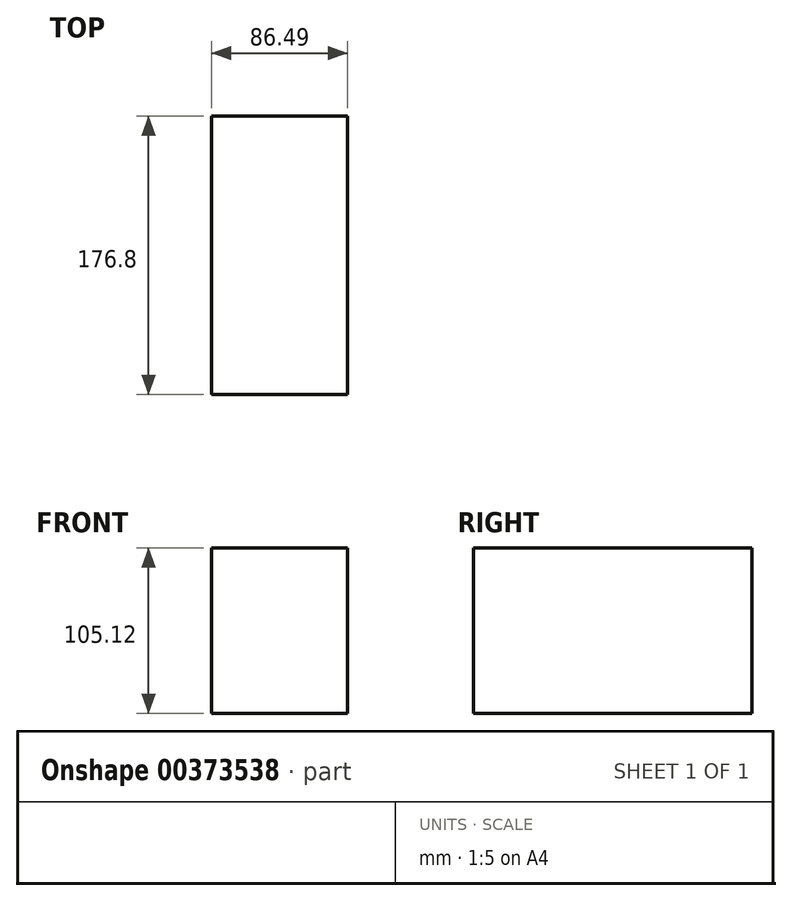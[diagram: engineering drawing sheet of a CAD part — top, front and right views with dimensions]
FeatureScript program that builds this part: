
annotation { "Feature Type Name" : "Feature", "Feature Type Description" : "" }
export const myFeature = defineFeature(function(context is Context, id is Id, definition is map)
    precondition{}
    {
        {
            var Q0;
            Q0=qCreatedBy(makeId("Front.planeOp"),FACE);
            var sketch = newSketch(context, id + "F0", { "sketchPlane" : qUnion([Q0])});
            skLineSegment(sketch, "E0.bottom", {"start": v(-41.12, 42.03) * mm, "end": v(45.37, 42.03) * mm});
            skLineSegment(sketch, "E0.top", {"start": v(-41.12, -38.09) * mm, "end": v(45.37, -38.09) * mm});
            skLineSegment(sketch, "E0.left", {"start": v(-41.12, 42.03) * mm, "end": v(-41.12, -38.09) * mm});
            skLineSegment(sketch, "E0.right", {"start": v(45.37, 42.03) * mm, "end": v(45.37, -38.09) * mm});
            skSolve(sketch);
        }
        {
            var Q0;
            Q0 = qSketchRegion(id + "F0", true);
            extrude(context, id + "F1", {"entities" : qUnion([Q0]), "depth" : 95.8 * mm});
        }
        {
            var Q0;
            Q0=makeQuery(id+"F1.opExtrude","SWEPT_FACE",FACE,{"disambiguationData":[OSD([sQuery(id+"F0.wireOp",EDGE,"E0.bottom")])]});
            extrude(context, id + "F2", {"entities" : qUnion([Q0]), "operationType" : NewBodyOperationType.ADD, "depth" : 25 * mm});
        }
        {
            var Q0;
            {var subQ0=sQuery(id+"F0.wireOp",EDGE,"E0.bottom");Q0=makeQuery(id+"F2.boolean.opBoolean","MERGE",FACE,{"derivedFrom":[makeQuery(id+"F1.opExtrude","CAP_FACE",FACE,{"disambiguationData":[OSD([subQ0,sQuery(id+"F0.wireOp",EDGE,"E0.top"),sQuery(id+"F0.wireOp",EDGE,"E0.left"),sQuery(id+"F0.wireOp",EDGE,"E0.right")])],"isStart":false}),makeQuery(id+"F2.opExtrude","SWEPT_FACE",FACE,{"disambiguationData":[OSD([subQ0]),TDD([makeQuery(id+"F1.opExtrude","CAP_EDGE",EDGE,{"disambiguationData":[OSD([subQ0])],"isStart":false})])]})]});}
            extrude(context, id + "F3", {"entities" : qUnion([Q0]), "operationType" : NewBodyOperationType.ADD, "depth" : 81 * mm});
        }
    });
